# Revit family: SAL 35
name_source: partatom
category: Air Terminals
revit_build: Autodesk Revit 2017 (Build: 20160225_1515(x64)
units: mm (PartAtom-declared; Revit-internal decimal feet)

## family parameters
Always vertical = Yes
Cut with Voids When Loaded = No
Part Type = Normal
Room Calculation Point = No
Round Connector Dimension = Use Diameter
Shared = No
Work Plane-Based = No

## types (64) — shared parameters
Lw dB(A) = 30/35/40
Max Flow = 0.0 L/s
Maß A = 44 mm  [stored 0.144357 ft]
Maß C = 60 mm  [stored 0.19685 ft]
Min Flow = 0.0 L/s
Product material = RAL 9016

## per-type parameters (varying)
- 500_1-reihig mit Anschlusskasten: Gewicht (g/m)=4360; Index=1; Index L=1; Index Reihig=1; L=500 mm  [stored 1.64042 ft]; Maß B=88 mm  [stored 0.288714 ft]; Maß E=25.3 mm  [stored 0.0830052 ft]; Maß F=34 mm; Maß H=227 mm  [stored 0.744751 ft]; Maß K=36 mm  [stored 0.11811 ft]; Maß M=61 mm  [stored 0.200131 ft]; Maß Ø D=123 mm  [stored 0.403543 ft]; Maß Ø D1=121 mm  [stored 0.396982 ft]; Mindest-abstand (m)=0.5/2.7/10.5; Stutzen (Stk.)=1; Visible 1 Reihig=Yes; Visible 1 Stutzen=Yes; Visible 2 Reihig=No; Visible 2 Stutzen=No; Visible 3 Reihig=No; Visible 4 Reihig=No; x krit (m)=8.0/10.5/13.3; y (m)=1.6/2.2/2.7; Δp (Pa) 1=15/23/33; Δp (Pa) 2=21/32/45
- 500_2-reihig mit Anschlusskasten: Gewicht (g/m)=5585; Index=1; Index L=1; Index Reihig=2; L=500 mm  [stored 1.64042 ft]; Maß B=120 mm  [stored 0.393701 ft]; Maß E=57.4 mm  [stored 0.18832 ft]; Maß F=67 mm; Maß H=242 mm  [stored 0.793963 ft]; Maß K=69 mm  [stored 0.226378 ft]; Maß M=92 mm  [stored 0.301837 ft]; Maß Ø D=138 mm  [stored 0.452756 ft]; Maß Ø D1=136 mm  [stored 0.446194 ft]; Mindest-abstand (m)=3.3/12.0/>15.0; Stutzen (Stk.)=1; Visible 1 Reihig=No; Visible 1 Stutzen=Yes; Visible 2 Reihig=Yes; Visible 2 Stutzen=No; Visible 3 Reihig=No; Visible 4 Reihig=No; x krit (m)=10.6/13.8/>15.0; y (m)=2.3/2.9/3.6; Δp (Pa) 1=12/18/27; Δp (Pa) 2=18/25/36
- 500_3-reihig mit Anschlusskasten: Gewicht (g/m)=6979; Index=1; Index L=1; Index Reihig=3; L=500 mm  [stored 1.64042 ft]; Maß B=152 mm  [stored 0.498688 ft]; Maß E=89.5 mm  [stored 0.293635 ft]; Maß F=99 mm  [stored 0.324803 ft]; Maß H=262 mm  [stored 0.85958 ft]; Maß K=101 mm  [stored 0.331365 ft]; Maß M=126 mm  [stored 0.413386 ft]; Maß Ø D=158 mm; Maß Ø D1=156 mm; Mindest-abstand (m)=8.0/>15.0/>15.0; Stutzen (Stk.)=1; Visible 1 Reihig=No; Visible 1 Stutzen=Yes; Visible 2 Reihig=No; Visible 2 Stutzen=No; Visible 3 Reihig=Yes; Visible 4 Reihig=No; x krit (m)=12.3/15.0/>15.0; y (m)=2.7/3.4/4.5; Δp (Pa) 1=10/15/23; Δp (Pa) 2=15/22/33
- 500_4-reihig mit Anschlusskasten: Gewicht (g/m)=8554; Index=1; Index L=1; Index Reihig=4; L=500 mm  [stored 1.64042 ft]; Maß B=184 mm  [stored 0.603675 ft]; Maß E=121.6 mm  [stored 0.39895 ft]; Maß F=132 mm  [stored 0.433071 ft]; Maß H=302 mm  [stored 0.990814 ft]; Maß K=134 mm; Maß M=158 mm; Maß Ø D=198 mm  [stored 0.649606 ft]; Maß Ø D1=196 mm  [stored 0.643045 ft]; Mindest-abstand (m)=11.0/>15.0/>15.0; Stutzen (Stk.)=1; Visible 1 Reihig=No; Visible 1 Stutzen=Yes; Visible 2 Reihig=No; Visible 2 Stutzen=No; Visible 3 Reihig=No; Visible 4 Reihig=Yes; x krit (m)=13.4/>15.0/>15.0; y (m)=2.9/3.8/4.9; Δp (Pa) 1=9/14/21; Δp (Pa) 2=13/20/29
- 600_1-reihig mit Anschlusskasten: Gewicht (g/m)=4360; Index=1; Index L=2; Index Reihig=1; L=600 mm; Maß B=88 mm  [stored 0.288714 ft]; Maß E=25.3 mm  [stored 0.0830052 ft]; Maß F=34 mm; Maß H=227 mm  [stored 0.744751 ft]; Maß K=36 mm  [stored 0.11811 ft]; Maß M=61 mm  [stored 0.200131 ft]; Maß Ø D=123 mm  [stored 0.403543 ft]; Maß Ø D1=121 mm  [stored 0.396982 ft]; Mindest-abstand (m)=0.5/2.7/10.5; Stutzen (Stk.)=1; Visible 1 Reihig=Yes; Visible 1 Stutzen=Yes; Visible 2 Reihig=No; Visible 2 Stutzen=No; Visible 3 Reihig=No; Visible 4 Reihig=No; x krit (m)=8.0/10.5/13.3; y (m)=1.6/2.2/2.7; Δp (Pa) 1=15/23/33; Δp (Pa) 2=21/32/45
- 700_1-reihig mit Anschlusskasten: Gewicht (g/m)=4360; Index=1; Index L=3; Index Reihig=1; L=700 mm  [stored 2.29659 ft]; Maß B=88 mm  [stored 0.288714 ft]; Maß E=25.3 mm  [stored 0.0830052 ft]; Maß F=34 mm; Maß H=227 mm  [stored 0.744751 ft]; Maß K=36 mm  [stored 0.11811 ft]; Maß M=61 mm  [stored 0.200131 ft]; Maß Ø D=123 mm  [stored 0.403543 ft]; Maß Ø D1=121 mm  [stored 0.396982 ft]; Mindest-abstand (m)=0.5/2.7/10.5; Stutzen (Stk.)=1; Visible 1 Reihig=Yes; Visible 1 Stutzen=Yes; Visible 2 Reihig=No; Visible 2 Stutzen=No; Visible 3 Reihig=No; Visible 4 Reihig=No; x krit (m)=8.0/10.5/13.3; y (m)=1.6/2.2/2.7; Δp (Pa) 1=15/23/33; Δp (Pa) 2=21/32/45
- 800_1-reihig mit Anschlusskasten: Gewicht (g/m)=4360; Index=1; Index L=4; Index Reihig=1; L=800 mm  [stored 2.62467 ft]; Maß B=88 mm  [stored 0.288714 ft]; Maß E=25.3 mm  [stored 0.0830052 ft]; Maß F=34 mm; Maß H=227 mm  [stored 0.744751 ft]; Maß K=36 mm  [stored 0.11811 ft]; Maß M=61 mm  [stored 0.200131 ft]; Maß Ø D=123 mm  [stored 0.403543 ft]; Maß Ø D1=121 mm  [stored 0.396982 ft]; Mindest-abstand (m)=0.5/2.7/10.5; Stutzen (Stk.)=1; Visible 1 Reihig=Yes; Visible 1 Stutzen=Yes; Visible 2 Reihig=No; Visible 2 Stutzen=No; Visible 3 Reihig=No; Visible 4 Reihig=No; x krit (m)=8.0/10.5/13.3; y (m)=1.6/2.2/2.7; Δp (Pa) 1=15/23/33; Δp (Pa) 2=21/32/45
- 900_1-reihig mit Anschlusskasten: Gewicht (g/m)=4360; Index=1; Index L=5; Index Reihig=1; L=900 mm  [stored 2.95276 ft]; Maß B=88 mm  [stored 0.288714 ft]; Maß E=25.3 mm  [stored 0.0830052 ft]; Maß F=34 mm; Maß H=227 mm  [stored 0.744751 ft]; Maß K=36 mm  [stored 0.11811 ft]; Maß M=61 mm  [stored 0.200131 ft]; Maß Ø D=123 mm  [stored 0.403543 ft]; Maß Ø D1=121 mm  [stored 0.396982 ft]; Mindest-abstand (m)=0.5/2.7/10.5; Stutzen (Stk.)=1; Visible 1 Reihig=Yes; Visible 1 Stutzen=Yes; Visible 2 Reihig=No; Visible 2 Stutzen=No; Visible 3 Reihig=No; Visible 4 Reihig=No; x krit (m)=8.0/10.5/13.3; y (m)=1.6/2.2/2.7; Δp (Pa) 1=15/23/33; Δp (Pa) 2=21/32/45
- 1000_1-reihig mit Anschlusskasten: Gewicht (g/m)=4360; Index=1; Index L=6; Index Reihig=1; L=1000 mm  [stored 3.28084 ft]; Maß B=88 mm  [stored 0.288714 ft]; Maß E=25.3 mm  [stored 0.0830052 ft]; Maß F=34 mm; Maß H=227 mm  [stored 0.744751 ft]; Maß K=36 mm  [stored 0.11811 ft]; Maß M=61 mm  [stored 0.200131 ft]; Maß Ø D=123 mm  [stored 0.403543 ft]; Maß Ø D1=121 mm  [stored 0.396982 ft]; Mindest-abstand (m)=0.5/2.7/10.5; Stutzen (Stk.)=1; Visible 1 Reihig=Yes; Visible 1 Stutzen=Yes; Visible 2 Reihig=No; Visible 2 Stutzen=No; Visible 3 Reihig=No; Visible 4 Reihig=No; x krit (m)=8.0/10.5/13.3; y (m)=1.6/2.2/2.7; Δp (Pa) 1=15/23/33; Δp (Pa) 2=21/32/45
- 1100_1-reihig mit Anschlusskasten: Gewicht (g/m)=4360; Index=1; Index L=7; Index Reihig=1; L=1100 mm; Maß B=88 mm  [stored 0.288714 ft]; Maß E=25.3 mm  [stored 0.0830052 ft]; Maß F=34 mm; Maß H=227 mm  [stored 0.744751 ft]; Maß K=36 mm  [stored 0.11811 ft]; Maß M=61 mm  [stored 0.200131 ft]; Maß Ø D=123 mm  [stored 0.403543 ft]; Maß Ø D1=121 mm  [stored 0.396982 ft]; Mindest-abstand (m)=0.5/2.7/10.5; Stutzen (Stk.)=1; Visible 1 Reihig=Yes; Visible 1 Stutzen=Yes; Visible 2 Reihig=No; Visible 2 Stutzen=No; Visible 3 Reihig=No; Visible 4 Reihig=No; x krit (m)=8.0/10.5/13.3; y (m)=1.6/2.2/2.7; Δp (Pa) 1=15/23/33; Δp (Pa) 2=21/32/45
- 1200_1-reihig mit Anschlusskasten: Gewicht (g/m)=4360; Index=1; Index L=8; Index Reihig=1; L=1200 mm; Maß B=88 mm  [stored 0.288714 ft]; Maß E=25.3 mm  [stored 0.0830052 ft]; Maß F=34 mm; Maß H=227 mm  [stored 0.744751 ft]; Maß K=36 mm  [stored 0.11811 ft]; Maß M=61 mm  [stored 0.200131 ft]; Maß Ø D=123 mm  [stored 0.403543 ft]; Maß Ø D1=121 mm  [stored 0.396982 ft]; Mindest-abstand (m)=0.5/2.7/10.5; Stutzen (Stk.)=1; Visible 1 Reihig=Yes; Visible 1 Stutzen=Yes; Visible 2 Reihig=No; Visible 2 Stutzen=No; Visible 3 Reihig=No; Visible 4 Reihig=No; x krit (m)=8.0/10.5/13.3; y (m)=1.6/2.2/2.7; Δp (Pa) 1=15/23/33; Δp (Pa) 2=21/32/45
- 1300_1-reihig mit Anschlusskasten: Gewicht (g/m)=4360; Index=1; Index L=9; Index Reihig=1; L=1300 mm; Maß B=88 mm  [stored 0.288714 ft]; Maß E=25.3 mm  [stored 0.0830052 ft]; Maß F=34 mm; Maß H=227 mm  [stored 0.744751 ft]; Maß K=36 mm  [stored 0.11811 ft]; Maß M=61 mm  [stored 0.200131 ft]; Maß Ø D=123 mm  [stored 0.403543 ft]; Maß Ø D1=121 mm  [stored 0.396982 ft]; Mindest-abstand (m)=0.5/2.7/10.5; Stutzen (Stk.)=1; Visible 1 Reihig=Yes; Visible 1 Stutzen=Yes; Visible 2 Reihig=No; Visible 2 Stutzen=No; Visible 3 Reihig=No; Visible 4 Reihig=No; x krit (m)=8.0/10.5/13.3; y (m)=1.6/2.2/2.7; Δp (Pa) 1=15/23/33; Δp (Pa) 2=21/32/45
- 1400_1-reihig mit Anschlusskasten: Gewicht (g/m)=4360; Index=1; Index L=10; Index Reihig=1; L=1400 mm; Maß B=88 mm  [stored 0.288714 ft]; Maß E=25.3 mm  [stored 0.0830052 ft]; Maß F=34 mm; Maß H=227 mm  [stored 0.744751 ft]; Maß K=36 mm  [stored 0.11811 ft]; Maß M=61 mm  [stored 0.200131 ft]; Maß Ø D=123 mm  [stored 0.403543 ft]; Maß Ø D1=121 mm  [stored 0.396982 ft]; Mindest-abstand (m)=0.5/2.7/10.5; Stutzen (Stk.)=1; Visible 1 Reihig=Yes; Visible 1 Stutzen=Yes; Visible 2 Reihig=No; Visible 2 Stutzen=No; Visible 3 Reihig=No; Visible 4 Reihig=No; x krit (m)=8.0/10.5/13.3; y (m)=1.6/2.2/2.7; Δp (Pa) 1=15/23/33; Δp (Pa) 2=21/32/45
- 1500_1-reihig mit Anschlusskasten: Gewicht (g/m)=4360; Index=1; Index L=11; Index Reihig=1; L=1500 mm; Maß B=88 mm  [stored 0.288714 ft]; Maß E=25.3 mm  [stored 0.0830052 ft]; Maß F=34 mm; Maß H=227 mm  [stored 0.744751 ft]; Maß K=36 mm  [stored 0.11811 ft]; Maß M=61 mm  [stored 0.200131 ft]; Maß Ø D=123 mm  [stored 0.403543 ft]; Maß Ø D1=121 mm  [stored 0.396982 ft]; Mindest-abstand (m)=0.5/2.7/10.5; Stutzen (Stk.)=1; Visible 1 Reihig=Yes; Visible 1 Stutzen=Yes; Visible 2 Reihig=No; Visible 2 Stutzen=No; Visible 3 Reihig=No; Visible 4 Reihig=No; x krit (m)=8.0/10.5/13.3; y (m)=1.6/2.2/2.7; Δp (Pa) 1=15/23/33; Δp (Pa) 2=21/32/45
- 1600_1-reihig mit Anschlusskasten: Gewicht (g/m)=4360; Index=2; Index L=12; Index Reihig=1; L=1600 mm; Maß B=88 mm  [stored 0.288714 ft]; Maß E=25.3 mm  [stored 0.0830052 ft]; Maß F=34 mm; Maß H=227 mm  [stored 0.744751 ft]; Maß K=36 mm  [stored 0.11811 ft]; Maß M=61 mm  [stored 0.200131 ft]; Maß Ø D=123 mm  [stored 0.403543 ft]; Maß Ø D1=121 mm  [stored 0.396982 ft]; Mindest-abstand (m)=0.5/2.7/10.5; Stutzen (Stk.)=2; Visible 1 Reihig=Yes; Visible 1 Stutzen=No; Visible 2 Reihig=No; Visible 2 Stutzen=Yes; Visible 3 Reihig=No; Visible 4 Reihig=No; x krit (m)=8.0/10.5/13.3; y (m)=1.6/2.2/2.7; Δp (Pa) 1=15/23/33; Δp (Pa) 2=21/32/45
- 1700_1-reihig mit Anschlusskasten: Gewicht (g/m)=4360; Index=2; Index L=13; Index Reihig=1; L=1700 mm; Maß B=88 mm  [stored 0.288714 ft]; Maß E=25.3 mm  [stored 0.0830052 ft]; Maß F=34 mm; Maß H=227 mm  [stored 0.744751 ft]; Maß K=36 mm  [stored 0.11811 ft]; Maß M=61 mm  [stored 0.200131 ft]; Maß Ø D=123 mm  [stored 0.403543 ft]; Maß Ø D1=121 mm  [stored 0.396982 ft]; Mindest-abstand (m)=0.5/2.7/10.5; Stutzen (Stk.)=2; Visible 1 Reihig=Yes; Visible 1 Stutzen=No; Visible 2 Reihig=No; Visible 2 Stutzen=Yes; Visible 3 Reihig=No; Visible 4 Reihig=No; x krit (m)=8.0/10.5/13.3; y (m)=1.6/2.2/2.7; Δp (Pa) 1=15/23/33; Δp (Pa) 2=21/32/45
- 1800_1-reihig mit Anschlusskasten: Gewicht (g/m)=4360; Index=2; Index L=14; Index Reihig=1; L=1800 mm; Maß B=88 mm  [stored 0.288714 ft]; Maß E=25.3 mm  [stored 0.0830052 ft]; Maß F=34 mm; Maß H=227 mm  [stored 0.744751 ft]; Maß K=36 mm  [stored 0.11811 ft]; Maß M=61 mm  [stored 0.200131 ft]; Maß Ø D=123 mm  [stored 0.403543 ft]; Maß Ø D1=121 mm  [stored 0.396982 ft]; Mindest-abstand (m)=0.5/2.7/10.5; Stutzen (Stk.)=2; Visible 1 Reihig=Yes; Visible 1 Stutzen=No; Visible 2 Reihig=No; Visible 2 Stutzen=Yes; Visible 3 Reihig=No; Visible 4 Reihig=No; x krit (m)=8.0/10.5/13.3; y (m)=1.6/2.2/2.7; Δp (Pa) 1=15/23/33; Δp (Pa) 2=21/32/45
- 1900_1-reihig mit Anschlusskasten: Gewicht (g/m)=4360; Index=2; Index L=15; Index Reihig=1; L=1900 mm; Maß B=88 mm  [stored 0.288714 ft]; Maß E=25.3 mm  [stored 0.0830052 ft]; Maß F=34 mm; Maß H=227 mm  [stored 0.744751 ft]; Maß K=36 mm  [stored 0.11811 ft]; Maß M=61 mm  [stored 0.200131 ft]; Maß Ø D=123 mm  [stored 0.403543 ft]; Maß Ø D1=121 mm  [stored 0.396982 ft]; Mindest-abstand (m)=0.5/2.7/10.5; Stutzen (Stk.)=2; Visible 1 Reihig=Yes; Visible 1 Stutzen=No; Visible 2 Reihig=No; Visible 2 Stutzen=Yes; Visible 3 Reihig=No; Visible 4 Reihig=No; x krit (m)=8.0/10.5/13.3; y (m)=1.6/2.2/2.7; Δp (Pa) 1=15/23/33; Δp (Pa) 2=21/32/45
- 2000_1-reihig mit Anschlusskasten: Gewicht (g/m)=4360; Index=2; Index L=16; Index Reihig=1; L=2000 mm; Maß B=88 mm  [stored 0.288714 ft]; Maß E=25.3 mm  [stored 0.0830052 ft]; Maß F=34 mm; Maß H=227 mm  [stored 0.744751 ft]; Maß K=36 mm  [stored 0.11811 ft]; Maß M=61 mm  [stored 0.200131 ft]; Maß Ø D=123 mm  [stored 0.403543 ft]; Maß Ø D1=121 mm  [stored 0.396982 ft]; Mindest-abstand (m)=0.5/2.7/10.5; Stutzen (Stk.)=2; Visible 1 Reihig=Yes; Visible 1 Stutzen=No; Visible 2 Reihig=No; Visible 2 Stutzen=Yes; Visible 3 Reihig=No; Visible 4 Reihig=No; x krit (m)=8.0/10.5/13.3; y (m)=1.6/2.2/2.7; Δp (Pa) 1=15/23/33; Δp (Pa) 2=21/32/45
- 600_2-reihig mit Anschlusskasten: Gewicht (g/m)=5585; Index=1; Index L=2; Index Reihig=2; L=600 mm; Maß B=120 mm  [stored 0.393701 ft]; Maß E=57.4 mm  [stored 0.18832 ft]; Maß F=67 mm; Maß H=242 mm  [stored 0.793963 ft]; Maß K=69 mm  [stored 0.226378 ft]; Maß M=92 mm  [stored 0.301837 ft]; Maß Ø D=138 mm  [stored 0.452756 ft]; Maß Ø D1=136 mm  [stored 0.446194 ft]; Mindest-abstand (m)=3.3/12.0/>15.0; Stutzen (Stk.)=1; Visible 1 Reihig=No; Visible 1 Stutzen=Yes; Visible 2 Reihig=Yes; Visible 2 Stutzen=No; Visible 3 Reihig=No; Visible 4 Reihig=No; x krit (m)=10.6/13.8/>15.0; y (m)=2.3/2.9/3.6; Δp (Pa) 1=12/18/27; Δp (Pa) 2=18/25/36
- 600_3-reihig mit Anschlusskasten: Gewicht (g/m)=6979; Index=1; Index L=2; Index Reihig=3; L=600 mm; Maß B=152 mm  [stored 0.498688 ft]; Maß E=89.5 mm  [stored 0.293635 ft]; Maß F=99 mm  [stored 0.324803 ft]; Maß H=262 mm  [stored 0.85958 ft]; Maß K=101 mm  [stored 0.331365 ft]; Maß M=126 mm  [stored 0.413386 ft]; Maß Ø D=158 mm; Maß Ø D1=156 mm; Mindest-abstand (m)=8.0/>15.0/>15.0; Stutzen (Stk.)=1; Visible 1 Reihig=No; Visible 1 Stutzen=Yes; Visible 2 Reihig=No; Visible 2 Stutzen=No; Visible 3 Reihig=Yes; Visible 4 Reihig=No; x krit (m)=12.3/15.0/>15.0; y (m)=2.7/3.4/4.5; Δp (Pa) 1=10/15/23; Δp (Pa) 2=15/22/33
- 600_4-reihig mit Anschlusskasten: Gewicht (g/m)=8554; Index=1; Index L=2; Index Reihig=4; L=600 mm; Maß B=184 mm  [stored 0.603675 ft]; Maß E=121.6 mm  [stored 0.39895 ft]; Maß F=132 mm  [stored 0.433071 ft]; Maß H=302 mm  [stored 0.990814 ft]; Maß K=134 mm; Maß M=158 mm; Maß Ø D=198 mm  [stored 0.649606 ft]; Maß Ø D1=196 mm  [stored 0.643045 ft]; Mindest-abstand (m)=11.0/>15.0/>15.0; Stutzen (Stk.)=1; Visible 1 Reihig=No; Visible 1 Stutzen=Yes; Visible 2 Reihig=No; Visible 2 Stutzen=No; Visible 3 Reihig=No; Visible 4 Reihig=Yes; x krit (m)=13.4/>15.0/>15.0; y (m)=2.9/3.8/4.9; Δp (Pa) 1=9/14/21; Δp (Pa) 2=13/20/29
- 700_2-reihig mit Anschlusskasten: Gewicht (g/m)=5585; Index=1; Index L=3; Index Reihig=2; L=700 mm  [stored 2.29659 ft]; Maß B=120 mm  [stored 0.393701 ft]; Maß E=57.4 mm  [stored 0.18832 ft]; Maß F=67 mm; Maß H=242 mm  [stored 0.793963 ft]; Maß K=69 mm  [stored 0.226378 ft]; Maß M=92 mm  [stored 0.301837 ft]; Maß Ø D=138 mm  [stored 0.452756 ft]; Maß Ø D1=136 mm  [stored 0.446194 ft]; Mindest-abstand (m)=3.3/12.0/>15.0; Stutzen (Stk.)=1; Visible 1 Reihig=No; Visible 1 Stutzen=Yes; Visible 2 Reihig=Yes; Visible 2 Stutzen=No; Visible 3 Reihig=No; Visible 4 Reihig=No; x krit (m)=10.6/13.8/>15.0; y (m)=2.3/2.9/3.6; Δp (Pa) 1=12/18/27; Δp (Pa) 2=18/25/36
- 700_3-reihig mit Anschlusskasten: Gewicht (g/m)=6979; Index=1; Index L=3; Index Reihig=3; L=700 mm  [stored 2.29659 ft]; Maß B=152 mm  [stored 0.498688 ft]; Maß E=89.5 mm  [stored 0.293635 ft]; Maß F=99 mm  [stored 0.324803 ft]; Maß H=262 mm  [stored 0.85958 ft]; Maß K=101 mm  [stored 0.331365 ft]; Maß M=126 mm  [stored 0.413386 ft]; Maß Ø D=158 mm; Maß Ø D1=156 mm; Mindest-abstand (m)=8.0/>15.0/>15.0; Stutzen (Stk.)=1; Visible 1 Reihig=No; Visible 1 Stutzen=Yes; Visible 2 Reihig=No; Visible 2 Stutzen=No; Visible 3 Reihig=Yes; Visible 4 Reihig=No; x krit (m)=12.3/15.0/>15.0; y (m)=2.7/3.4/4.5; Δp (Pa) 1=10/15/23; Δp (Pa) 2=15/22/33
- 700_4-reihig mit Anschlusskasten: Gewicht (g/m)=8554; Index=1; Index L=3; Index Reihig=4; L=700 mm  [stored 2.29659 ft]; Maß B=184 mm  [stored 0.603675 ft]; Maß E=121.6 mm  [stored 0.39895 ft]; Maß F=132 mm  [stored 0.433071 ft]; Maß H=302 mm  [stored 0.990814 ft]; Maß K=134 mm; Maß M=158 mm; Maß Ø D=198 mm  [stored 0.649606 ft]; Maß Ø D1=196 mm  [stored 0.643045 ft]; Mindest-abstand (m)=11.0/>15.0/>15.0; Stutzen (Stk.)=1; Visible 1 Reihig=No; Visible 1 Stutzen=Yes; Visible 2 Reihig=No; Visible 2 Stutzen=No; Visible 3 Reihig=No; Visible 4 Reihig=Yes; x krit (m)=13.4/>15.0/>15.0; y (m)=2.9/3.8/4.9; Δp (Pa) 1=9/14/21; Δp (Pa) 2=13/20/29
- 800_2-reihig mit Anschlusskasten: Gewicht (g/m)=5585; Index=1; Index L=4; Index Reihig=2; L=800 mm  [stored 2.62467 ft]; Maß B=120 mm  [stored 0.393701 ft]; Maß E=57.4 mm  [stored 0.18832 ft]; Maß F=67 mm; Maß H=242 mm  [stored 0.793963 ft]; Maß K=69 mm  [stored 0.226378 ft]; Maß M=92 mm  [stored 0.301837 ft]; Maß Ø D=138 mm  [stored 0.452756 ft]; Maß Ø D1=136 mm  [stored 0.446194 ft]; Mindest-abstand (m)=3.3/12.0/>15.0; Stutzen (Stk.)=1; Visible 1 Reihig=No; Visible 1 Stutzen=Yes; Visible 2 Reihig=Yes; Visible 2 Stutzen=No; Visible 3 Reihig=No; Visible 4 Reihig=No; x krit (m)=10.6/13.8/>15.0; y (m)=2.3/2.9/3.6; Δp (Pa) 1=12/18/27; Δp (Pa) 2=18/25/36
- 800_3-reihig mit Anschlusskasten: Gewicht (g/m)=6979; Index=1; Index L=4; Index Reihig=3; L=800 mm  [stored 2.62467 ft]; Maß B=152 mm  [stored 0.498688 ft]; Maß E=89.5 mm  [stored 0.293635 ft]; Maß F=99 mm  [stored 0.324803 ft]; Maß H=262 mm  [stored 0.85958 ft]; Maß K=101 mm  [stored 0.331365 ft]; Maß M=126 mm  [stored 0.413386 ft]; Maß Ø D=158 mm; Maß Ø D1=156 mm; Mindest-abstand (m)=8.0/>15.0/>15.0; Stutzen (Stk.)=1; Visible 1 Reihig=No; Visible 1 Stutzen=Yes; Visible 2 Reihig=No; Visible 2 Stutzen=No; Visible 3 Reihig=Yes; Visible 4 Reihig=No; x krit (m)=12.3/15.0/>15.0; y (m)=2.7/3.4/4.5; Δp (Pa) 1=10/15/23; Δp (Pa) 2=15/22/33
- 800_4-reihig mit Anschlusskasten: Gewicht (g/m)=8554; Index=1; Index L=4; Index Reihig=4; L=800 mm  [stored 2.62467 ft]; Maß B=184 mm  [stored 0.603675 ft]; Maß E=121.6 mm  [stored 0.39895 ft]; Maß F=132 mm  [stored 0.433071 ft]; Maß H=302 mm  [stored 0.990814 ft]; Maß K=134 mm; Maß M=158 mm; Maß Ø D=198 mm  [stored 0.649606 ft]; Maß Ø D1=196 mm  [stored 0.643045 ft]; Mindest-abstand (m)=11.0/>15.0/>15.0; Stutzen (Stk.)=1; Visible 1 Reihig=No; Visible 1 Stutzen=Yes; Visible 2 Reihig=No; Visible 2 Stutzen=No; Visible 3 Reihig=No; Visible 4 Reihig=Yes; x krit (m)=13.4/>15.0/>15.0; y (m)=2.9/3.8/4.9; Δp (Pa) 1=9/14/21; Δp (Pa) 2=13/20/29
- 900_2-reihig mit Anschlusskasten: Gewicht (g/m)=5585; Index=1; Index L=5; Index Reihig=2; L=900 mm  [stored 2.95276 ft]; Maß B=120 mm  [stored 0.393701 ft]; Maß E=57.4 mm  [stored 0.18832 ft]; Maß F=67 mm; Maß H=242 mm  [stored 0.793963 ft]; Maß K=69 mm  [stored 0.226378 ft]; Maß M=92 mm  [stored 0.301837 ft]; Maß Ø D=138 mm  [stored 0.452756 ft]; Maß Ø D1=136 mm  [stored 0.446194 ft]; Mindest-abstand (m)=3.3/12.0/>15.0; Stutzen (Stk.)=1; Visible 1 Reihig=No; Visible 1 Stutzen=Yes; Visible 2 Reihig=Yes; Visible 2 Stutzen=No; Visible 3 Reihig=No; Visible 4 Reihig=No; x krit (m)=10.6/13.8/>15.0; y (m)=2.3/2.9/3.6; Δp (Pa) 1=12/18/27; Δp (Pa) 2=18/25/36
- 900_3-reihig mit Anschlusskasten: Gewicht (g/m)=6979; Index=1; Index L=5; Index Reihig=3; L=900 mm  [stored 2.95276 ft]; Maß B=152 mm  [stored 0.498688 ft]; Maß E=89.5 mm  [stored 0.293635 ft]; Maß F=99 mm  [stored 0.324803 ft]; Maß H=262 mm  [stored 0.85958 ft]; Maß K=101 mm  [stored 0.331365 ft]; Maß M=126 mm  [stored 0.413386 ft]; Maß Ø D=158 mm; Maß Ø D1=156 mm; Mindest-abstand (m)=8.0/>15.0/>15.0; Stutzen (Stk.)=1; Visible 1 Reihig=No; Visible 1 Stutzen=Yes; Visible 2 Reihig=No; Visible 2 Stutzen=No; Visible 3 Reihig=Yes; Visible 4 Reihig=No; x krit (m)=12.3/15.0/>15.0; y (m)=2.7/3.4/4.5; Δp (Pa) 1=10/15/23; Δp (Pa) 2=15/22/33
- 900_4-reihig mit Anschlusskasten: Gewicht (g/m)=8554; Index=1; Index L=5; Index Reihig=4; L=900 mm  [stored 2.95276 ft]; Maß B=184 mm  [stored 0.603675 ft]; Maß E=121.6 mm  [stored 0.39895 ft]; Maß F=132 mm  [stored 0.433071 ft]; Maß H=302 mm  [stored 0.990814 ft]; Maß K=134 mm; Maß M=158 mm; Maß Ø D=198 mm  [stored 0.649606 ft]; Maß Ø D1=196 mm  [stored 0.643045 ft]; Mindest-abstand (m)=11.0/>15.0/>15.0; Stutzen (Stk.)=1; Visible 1 Reihig=No; Visible 1 Stutzen=Yes; Visible 2 Reihig=No; Visible 2 Stutzen=No; Visible 3 Reihig=No; Visible 4 Reihig=Yes; x krit (m)=13.4/>15.0/>15.0; y (m)=2.9/3.8/4.9; Δp (Pa) 1=9/14/21; Δp (Pa) 2=13/20/29
- 1000_2-reihig mit Anschlusskasten: Gewicht (g/m)=5585; Index=1; Index L=6; Index Reihig=2; L=1000 mm  [stored 3.28084 ft]; Maß B=120 mm  [stored 0.393701 ft]; Maß E=57.4 mm  [stored 0.18832 ft]; Maß F=67 mm; Maß H=242 mm  [stored 0.793963 ft]; Maß K=69 mm  [stored 0.226378 ft]; Maß M=92 mm  [stored 0.301837 ft]; Maß Ø D=138 mm  [stored 0.452756 ft]; Maß Ø D1=136 mm  [stored 0.446194 ft]; Mindest-abstand (m)=3.3/12.0/>15.0; Stutzen (Stk.)=1; Visible 1 Reihig=No; Visible 1 Stutzen=Yes; Visible 2 Reihig=Yes; Visible 2 Stutzen=No; Visible 3 Reihig=No; Visible 4 Reihig=No; x krit (m)=10.6/13.8/>15.0; y (m)=2.3/2.9/3.6; Δp (Pa) 1=12/18/27; Δp (Pa) 2=18/25/36
- 1000_3-reihig mit Anschlusskasten: Gewicht (g/m)=6979; Index=1; Index L=6; Index Reihig=3; L=1000 mm  [stored 3.28084 ft]; Maß B=152 mm  [stored 0.498688 ft]; Maß E=89.5 mm  [stored 0.293635 ft]; Maß F=99 mm  [stored 0.324803 ft]; Maß H=262 mm  [stored 0.85958 ft]; Maß K=101 mm  [stored 0.331365 ft]; Maß M=126 mm  [stored 0.413386 ft]; Maß Ø D=158 mm; Maß Ø D1=156 mm; Mindest-abstand (m)=8.0/>15.0/>15.0; Stutzen (Stk.)=1; Visible 1 Reihig=No; Visible 1 Stutzen=Yes; Visible 2 Reihig=No; Visible 2 Stutzen=No; Visible 3 Reihig=Yes; Visible 4 Reihig=No; x krit (m)=12.3/15.0/>15.0; y (m)=2.7/3.4/4.5; Δp (Pa) 1=10/15/23; Δp (Pa) 2=15/22/33
- 1000_4-reihig mit Anschlusskasten: Gewicht (g/m)=8554; Index=1; Index L=6; Index Reihig=4; L=1000 mm  [stored 3.28084 ft]; Maß B=184 mm  [stored 0.603675 ft]; Maß E=121.6 mm  [stored 0.39895 ft]; Maß F=132 mm  [stored 0.433071 ft]; Maß H=302 mm  [stored 0.990814 ft]; Maß K=134 mm; Maß M=158 mm; Maß Ø D=198 mm  [stored 0.649606 ft]; Maß Ø D1=196 mm  [stored 0.643045 ft]; Mindest-abstand (m)=11.0/>15.0/>15.0; Stutzen (Stk.)=1; Visible 1 Reihig=No; Visible 1 Stutzen=Yes; Visible 2 Reihig=No; Visible 2 Stutzen=No; Visible 3 Reihig=No; Visible 4 Reihig=Yes; x krit (m)=13.4/>15.0/>15.0; y (m)=2.9/3.8/4.9; Δp (Pa) 1=9/14/21; Δp (Pa) 2=13/20/29
- 1100_2-reihig mit Anschlusskasten: Gewicht (g/m)=5585; Index=1; Index L=7; Index Reihig=2; L=1100 mm; Maß B=120 mm  [stored 0.393701 ft]; Maß E=57.4 mm  [stored 0.18832 ft]; Maß F=67 mm; Maß H=242 mm  [stored 0.793963 ft]; Maß K=69 mm  [stored 0.226378 ft]; Maß M=92 mm  [stored 0.301837 ft]; Maß Ø D=138 mm  [stored 0.452756 ft]; Maß Ø D1=136 mm  [stored 0.446194 ft]; Mindest-abstand (m)=3.3/12.0/>15.0; Stutzen (Stk.)=1; Visible 1 Reihig=No; Visible 1 Stutzen=Yes; Visible 2 Reihig=Yes; Visible 2 Stutzen=No; Visible 3 Reihig=No; Visible 4 Reihig=No; x krit (m)=10.6/13.8/>15.0; y (m)=2.3/2.9/3.6; Δp (Pa) 1=12/18/27; Δp (Pa) 2=18/25/36
- 1100_3-reihig mit Anschlusskasten: Gewicht (g/m)=6979; Index=1; Index L=7; Index Reihig=3; L=1100 mm; Maß B=152 mm  [stored 0.498688 ft]; Maß E=89.5 mm  [stored 0.293635 ft]; Maß F=99 mm  [stored 0.324803 ft]; Maß H=262 mm  [stored 0.85958 ft]; Maß K=101 mm  [stored 0.331365 ft]; Maß M=126 mm  [stored 0.413386 ft]; Maß Ø D=158 mm; Maß Ø D1=156 mm; Mindest-abstand (m)=8.0/>15.0/>15.0; Stutzen (Stk.)=1; Visible 1 Reihig=No; Visible 1 Stutzen=Yes; Visible 2 Reihig=No; Visible 2 Stutzen=No; Visible 3 Reihig=Yes; Visible 4 Reihig=No; x krit (m)=12.3/15.0/>15.0; y (m)=2.7/3.4/4.5; Δp (Pa) 1=10/15/23; Δp (Pa) 2=15/22/33
- 1100_4-reihig mit Anschlusskasten: Gewicht (g/m)=8554; Index=1; Index L=7; Index Reihig=4; L=1100 mm; Maß B=184 mm  [stored 0.603675 ft]; Maß E=121.6 mm  [stored 0.39895 ft]; Maß F=132 mm  [stored 0.433071 ft]; Maß H=302 mm  [stored 0.990814 ft]; Maß K=134 mm; Maß M=158 mm; Maß Ø D=198 mm  [stored 0.649606 ft]; Maß Ø D1=196 mm  [stored 0.643045 ft]; Mindest-abstand (m)=11.0/>15.0/>15.0; Stutzen (Stk.)=1; Visible 1 Reihig=No; Visible 1 Stutzen=Yes; Visible 2 Reihig=No; Visible 2 Stutzen=No; Visible 3 Reihig=No; Visible 4 Reihig=Yes; x krit (m)=13.4/>15.0/>15.0; y (m)=2.9/3.8/4.9; Δp (Pa) 1=9/14/21; Δp (Pa) 2=13/20/29
- 1200_2-reihig mit Anschlusskasten: Gewicht (g/m)=5585; Index=1; Index L=8; Index Reihig=2; L=1200 mm; Maß B=120 mm  [stored 0.393701 ft]; Maß E=57.4 mm  [stored 0.18832 ft]; Maß F=67 mm; Maß H=242 mm  [stored 0.793963 ft]; Maß K=69 mm  [stored 0.226378 ft]; Maß M=92 mm  [stored 0.301837 ft]; Maß Ø D=138 mm  [stored 0.452756 ft]; Maß Ø D1=136 mm  [stored 0.446194 ft]; Mindest-abstand (m)=3.3/12.0/>15.0; Stutzen (Stk.)=1; Visible 1 Reihig=No; Visible 1 Stutzen=Yes; Visible 2 Reihig=Yes; Visible 2 Stutzen=No; Visible 3 Reihig=No; Visible 4 Reihig=No; x krit (m)=10.6/13.8/>15.0; y (m)=2.3/2.9/3.6; Δp (Pa) 1=12/18/27; Δp (Pa) 2=18/25/36
- 1200_3-reihig mit Anschlusskasten: Gewicht (g/m)=6979; Index=1; Index L=8; Index Reihig=3; L=1200 mm; Maß B=152 mm  [stored 0.498688 ft]; Maß E=89.5 mm  [stored 0.293635 ft]; Maß F=99 mm  [stored 0.324803 ft]; Maß H=262 mm  [stored 0.85958 ft]; Maß K=101 mm  [stored 0.331365 ft]; Maß M=126 mm  [stored 0.413386 ft]; Maß Ø D=158 mm; Maß Ø D1=156 mm; Mindest-abstand (m)=8.0/>15.0/>15.0; Stutzen (Stk.)=1; Visible 1 Reihig=No; Visible 1 Stutzen=Yes; Visible 2 Reihig=No; Visible 2 Stutzen=No; Visible 3 Reihig=Yes; Visible 4 Reihig=No; x krit (m)=12.3/15.0/>15.0; y (m)=2.7/3.4/4.5; Δp (Pa) 1=10/15/23; Δp (Pa) 2=15/22/33
- 1200_4-reihig mit Anschlusskasten: Gewicht (g/m)=8554; Index=1; Index L=8; Index Reihig=4; L=1200 mm; Maß B=184 mm  [stored 0.603675 ft]; Maß E=121.6 mm  [stored 0.39895 ft]; Maß F=132 mm  [stored 0.433071 ft]; Maß H=302 mm  [stored 0.990814 ft]; Maß K=134 mm; Maß M=158 mm; Maß Ø D=198 mm  [stored 0.649606 ft]; Maß Ø D1=196 mm  [stored 0.643045 ft]; Mindest-abstand (m)=11.0/>15.0/>15.0; Stutzen (Stk.)=1; Visible 1 Reihig=No; Visible 1 Stutzen=Yes; Visible 2 Reihig=No; Visible 2 Stutzen=No; Visible 3 Reihig=No; Visible 4 Reihig=Yes; x krit (m)=13.4/>15.0/>15.0; y (m)=2.9/3.8/4.9; Δp (Pa) 1=9/14/21; Δp (Pa) 2=13/20/29
- 1300_2-reihig mit Anschlusskasten: Gewicht (g/m)=5585; Index=1; Index L=9; Index Reihig=2; L=1300 mm; Maß B=120 mm  [stored 0.393701 ft]; Maß E=57.4 mm  [stored 0.18832 ft]; Maß F=67 mm; Maß H=242 mm  [stored 0.793963 ft]; Maß K=69 mm  [stored 0.226378 ft]; Maß M=92 mm  [stored 0.301837 ft]; Maß Ø D=138 mm  [stored 0.452756 ft]; Maß Ø D1=136 mm  [stored 0.446194 ft]; Mindest-abstand (m)=3.3/12.0/>15.0; Stutzen (Stk.)=1; Visible 1 Reihig=No; Visible 1 Stutzen=Yes; Visible 2 Reihig=Yes; Visible 2 Stutzen=No; Visible 3 Reihig=No; Visible 4 Reihig=No; x krit (m)=10.6/13.8/>15.0; y (m)=2.3/2.9/3.6; Δp (Pa) 1=12/18/27; Δp (Pa) 2=18/25/36
- 1300_3-reihig mit Anschlusskasten: Gewicht (g/m)=6979; Index=1; Index L=9; Index Reihig=3; L=1300 mm; Maß B=152 mm  [stored 0.498688 ft]; Maß E=89.5 mm  [stored 0.293635 ft]; Maß F=99 mm  [stored 0.324803 ft]; Maß H=262 mm  [stored 0.85958 ft]; Maß K=101 mm  [stored 0.331365 ft]; Maß M=126 mm  [stored 0.413386 ft]; Maß Ø D=158 mm; Maß Ø D1=156 mm; Mindest-abstand (m)=8.0/>15.0/>15.0; Stutzen (Stk.)=1; Visible 1 Reihig=No; Visible 1 Stutzen=Yes; Visible 2 Reihig=No; Visible 2 Stutzen=No; Visible 3 Reihig=Yes; Visible 4 Reihig=No; x krit (m)=12.3/15.0/>15.0; y (m)=2.7/3.4/4.5; Δp (Pa) 1=10/15/23; Δp (Pa) 2=15/22/33
- 1300_4-reihig mit Anschlusskasten: Gewicht (g/m)=8554; Index=1; Index L=9; Index Reihig=4; L=1300 mm; Maß B=184 mm  [stored 0.603675 ft]; Maß E=121.6 mm  [stored 0.39895 ft]; Maß F=132 mm  [stored 0.433071 ft]; Maß H=302 mm  [stored 0.990814 ft]; Maß K=134 mm; Maß M=158 mm; Maß Ø D=198 mm  [stored 0.649606 ft]; Maß Ø D1=196 mm  [stored 0.643045 ft]; Mindest-abstand (m)=11.0/>15.0/>15.0; Stutzen (Stk.)=1; Visible 1 Reihig=No; Visible 1 Stutzen=Yes; Visible 2 Reihig=No; Visible 2 Stutzen=No; Visible 3 Reihig=No; Visible 4 Reihig=Yes; x krit (m)=13.4/>15.0/>15.0; y (m)=2.9/3.8/4.9; Δp (Pa) 1=9/14/21; Δp (Pa) 2=13/20/29
- 1400_2-reihig mit Anschlusskasten: Gewicht (g/m)=5585; Index=1; Index L=10; Index Reihig=2; L=1400 mm; Maß B=120 mm  [stored 0.393701 ft]; Maß E=57.4 mm  [stored 0.18832 ft]; Maß F=67 mm; Maß H=242 mm  [stored 0.793963 ft]; Maß K=69 mm  [stored 0.226378 ft]; Maß M=92 mm  [stored 0.301837 ft]; Maß Ø D=138 mm  [stored 0.452756 ft]; Maß Ø D1=136 mm  [stored 0.446194 ft]; Mindest-abstand (m)=3.3/12.0/>15.0; Stutzen (Stk.)=1; Visible 1 Reihig=No; Visible 1 Stutzen=Yes; Visible 2 Reihig=Yes; Visible 2 Stutzen=No; Visible 3 Reihig=No; Visible 4 Reihig=No; x krit (m)=10.6/13.8/>15.0; y (m)=2.3/2.9/3.6; Δp (Pa) 1=12/18/27; Δp (Pa) 2=18/25/36
- 1400_3-reihig mit Anschlusskasten: Gewicht (g/m)=6979; Index=1; Index L=10; Index Reihig=3; L=1400 mm; Maß B=152 mm  [stored 0.498688 ft]; Maß E=89.5 mm  [stored 0.293635 ft]; Maß F=99 mm  [stored 0.324803 ft]; Maß H=262 mm  [stored 0.85958 ft]; Maß K=101 mm  [stored 0.331365 ft]; Maß M=126 mm  [stored 0.413386 ft]; Maß Ø D=158 mm; Maß Ø D1=156 mm; Mindest-abstand (m)=8.0/>15.0/>15.0; Stutzen (Stk.)=1; Visible 1 Reihig=No; Visible 1 Stutzen=Yes; Visible 2 Reihig=No; Visible 2 Stutzen=No; Visible 3 Reihig=Yes; Visible 4 Reihig=No; x krit (m)=12.3/15.0/>15.0; y (m)=2.7/3.4/4.5; Δp (Pa) 1=10/15/23; Δp (Pa) 2=15/22/33
- 1400_4-reihig mit Anschlusskasten: Gewicht (g/m)=8554; Index=1; Index L=10; Index Reihig=4; L=1400 mm; Maß B=184 mm  [stored 0.603675 ft]; Maß E=121.6 mm  [stored 0.39895 ft]; Maß F=132 mm  [stored 0.433071 ft]; Maß H=302 mm  [stored 0.990814 ft]; Maß K=134 mm; Maß M=158 mm; Maß Ø D=198 mm  [stored 0.649606 ft]; Maß Ø D1=196 mm  [stored 0.643045 ft]; Mindest-abstand (m)=11.0/>15.0/>15.0; Stutzen (Stk.)=1; Visible 1 Reihig=No; Visible 1 Stutzen=Yes; Visible 2 Reihig=No; Visible 2 Stutzen=No; Visible 3 Reihig=No; Visible 4 Reihig=Yes; x krit (m)=13.4/>15.0/>15.0; y (m)=2.9/3.8/4.9; Δp (Pa) 1=9/14/21; Δp (Pa) 2=13/20/29
- 1500_2-reihig mit Anschlusskasten: Gewicht (g/m)=5585; Index=1; Index L=11; Index Reihig=2; L=1500 mm; Maß B=120 mm  [stored 0.393701 ft]; Maß E=57.4 mm  [stored 0.18832 ft]; Maß F=67 mm; Maß H=242 mm  [stored 0.793963 ft]; Maß K=69 mm  [stored 0.226378 ft]; Maß M=92 mm  [stored 0.301837 ft]; Maß Ø D=138 mm  [stored 0.452756 ft]; Maß Ø D1=136 mm  [stored 0.446194 ft]; Mindest-abstand (m)=3.3/12.0/>15.0; Stutzen (Stk.)=1; Visible 1 Reihig=No; Visible 1 Stutzen=Yes; Visible 2 Reihig=Yes; Visible 2 Stutzen=No; Visible 3 Reihig=No; Visible 4 Reihig=No; x krit (m)=10.6/13.8/>15.0; y (m)=2.3/2.9/3.6; Δp (Pa) 1=12/18/27; Δp (Pa) 2=18/25/36
- 1500_3-reihig mit Anschlusskasten: Gewicht (g/m)=6979; Index=1; Index L=11; Index Reihig=3; L=1500 mm; Maß B=152 mm  [stored 0.498688 ft]; Maß E=89.5 mm  [stored 0.293635 ft]; Maß F=99 mm  [stored 0.324803 ft]; Maß H=262 mm  [stored 0.85958 ft]; Maß K=101 mm  [stored 0.331365 ft]; Maß M=126 mm  [stored 0.413386 ft]; Maß Ø D=158 mm; Maß Ø D1=156 mm; Mindest-abstand (m)=8.0/>15.0/>15.0; Stutzen (Stk.)=1; Visible 1 Reihig=No; Visible 1 Stutzen=Yes; Visible 2 Reihig=No; Visible 2 Stutzen=No; Visible 3 Reihig=Yes; Visible 4 Reihig=No; x krit (m)=12.3/15.0/>15.0; y (m)=2.7/3.4/4.5; Δp (Pa) 1=10/15/23; Δp (Pa) 2=15/22/33
- 1500_4-reihig mit Anschlusskasten: Gewicht (g/m)=8554; Index=1; Index L=11; Index Reihig=4; L=1500 mm; Maß B=184 mm  [stored 0.603675 ft]; Maß E=121.6 mm  [stored 0.39895 ft]; Maß F=132 mm  [stored 0.433071 ft]; Maß H=302 mm  [stored 0.990814 ft]; Maß K=134 mm; Maß M=158 mm; Maß Ø D=198 mm  [stored 0.649606 ft]; Maß Ø D1=196 mm  [stored 0.643045 ft]; Mindest-abstand (m)=11.0/>15.0/>15.0; Stutzen (Stk.)=1; Visible 1 Reihig=No; Visible 1 Stutzen=Yes; Visible 2 Reihig=No; Visible 2 Stutzen=No; Visible 3 Reihig=No; Visible 4 Reihig=Yes; x krit (m)=13.4/>15.0/>15.0; y (m)=2.9/3.8/4.9; Δp (Pa) 1=9/14/21; Δp (Pa) 2=13/20/29
- 1600_2-reihig mit Anschlusskasten: Gewicht (g/m)=5585; Index=2; Index L=12; Index Reihig=2; L=1600 mm; Maß B=120 mm  [stored 0.393701 ft]; Maß E=57.4 mm  [stored 0.18832 ft]; Maß F=67 mm; Maß H=242 mm  [stored 0.793963 ft]; Maß K=69 mm  [stored 0.226378 ft]; Maß M=92 mm  [stored 0.301837 ft]; Maß Ø D=138 mm  [stored 0.452756 ft]; Maß Ø D1=136 mm  [stored 0.446194 ft]; Mindest-abstand (m)=3.3/12.0/>15.0; Stutzen (Stk.)=2; Visible 1 Reihig=No; Visible 1 Stutzen=No; Visible 2 Reihig=Yes; Visible 2 Stutzen=Yes; Visible 3 Reihig=No; Visible 4 Reihig=No; x krit (m)=10.6/13.8/>15.0; y (m)=2.3/2.9/3.6; Δp (Pa) 1=12/18/27; Δp (Pa) 2=18/25/36
- 1600_3-reihig mit Anschlusskasten: Gewicht (g/m)=6979; Index=2; Index L=12; Index Reihig=3; L=1600 mm; Maß B=152 mm  [stored 0.498688 ft]; Maß E=89.5 mm  [stored 0.293635 ft]; Maß F=99 mm  [stored 0.324803 ft]; Maß H=262 mm  [stored 0.85958 ft]; Maß K=101 mm  [stored 0.331365 ft]; Maß M=126 mm  [stored 0.413386 ft]; Maß Ø D=158 mm; Maß Ø D1=156 mm; Mindest-abstand (m)=8.0/>15.0/>15.0; Stutzen (Stk.)=2; Visible 1 Reihig=No; Visible 1 Stutzen=No; Visible 2 Reihig=No; Visible 2 Stutzen=Yes; Visible 3 Reihig=Yes; Visible 4 Reihig=No; x krit (m)=12.3/15.0/>15.0; y (m)=2.7/3.4/4.5; Δp (Pa) 1=10/15/23; Δp (Pa) 2=15/22/33
- 1600_4-reihig mit Anschlusskasten: Gewicht (g/m)=8554; Index=2; Index L=12; Index Reihig=4; L=1600 mm; Maß B=184 mm  [stored 0.603675 ft]; Maß E=121.6 mm  [stored 0.39895 ft]; Maß F=132 mm  [stored 0.433071 ft]; Maß H=302 mm  [stored 0.990814 ft]; Maß K=134 mm; Maß M=158 mm; Maß Ø D=198 mm  [stored 0.649606 ft]; Maß Ø D1=196 mm  [stored 0.643045 ft]; Mindest-abstand (m)=11.0/>15.0/>15.0; Stutzen (Stk.)=2; Visible 1 Reihig=No; Visible 1 Stutzen=No; Visible 2 Reihig=No; Visible 2 Stutzen=Yes; Visible 3 Reihig=No; Visible 4 Reihig=Yes; x krit (m)=13.4/>15.0/>15.0; y (m)=2.9/3.8/4.9; Δp (Pa) 1=9/14/21; Δp (Pa) 2=13/20/29
- 1700_2-reihig mit Anschlusskasten: Gewicht (g/m)=5585; Index=2; Index L=13; Index Reihig=2; L=1700 mm; Maß B=120 mm  [stored 0.393701 ft]; Maß E=57.4 mm  [stored 0.18832 ft]; Maß F=67 mm; Maß H=242 mm  [stored 0.793963 ft]; Maß K=69 mm  [stored 0.226378 ft]; Maß M=92 mm  [stored 0.301837 ft]; Maß Ø D=138 mm  [stored 0.452756 ft]; Maß Ø D1=136 mm  [stored 0.446194 ft]; Mindest-abstand (m)=3.3/12.0/>15.0; Stutzen (Stk.)=2; Visible 1 Reihig=No; Visible 1 Stutzen=No; Visible 2 Reihig=Yes; Visible 2 Stutzen=Yes; Visible 3 Reihig=No; Visible 4 Reihig=No; x krit (m)=10.6/13.8/>15.0; y (m)=2.3/2.9/3.6; Δp (Pa) 1=12/18/27; Δp (Pa) 2=18/25/36
- 1700_3-reihig mit Anschlusskasten: Gewicht (g/m)=6979; Index=2; Index L=13; Index Reihig=3; L=1700 mm; Maß B=152 mm  [stored 0.498688 ft]; Maß E=89.5 mm  [stored 0.293635 ft]; Maß F=99 mm  [stored 0.324803 ft]; Maß H=262 mm  [stored 0.85958 ft]; Maß K=101 mm  [stored 0.331365 ft]; Maß M=126 mm  [stored 0.413386 ft]; Maß Ø D=158 mm; Maß Ø D1=156 mm; Mindest-abstand (m)=8.0/>15.0/>15.0; Stutzen (Stk.)=2; Visible 1 Reihig=No; Visible 1 Stutzen=No; Visible 2 Reihig=No; Visible 2 Stutzen=Yes; Visible 3 Reihig=Yes; Visible 4 Reihig=No; x krit (m)=12.3/15.0/>15.0; y (m)=2.7/3.4/4.5; Δp (Pa) 1=10/15/23; Δp (Pa) 2=15/22/33
- 1700_4-reihig mit Anschlusskasten: Gewicht (g/m)=8554; Index=2; Index L=13; Index Reihig=4; L=1700 mm; Maß B=184 mm  [stored 0.603675 ft]; Maß E=121.6 mm  [stored 0.39895 ft]; Maß F=132 mm  [stored 0.433071 ft]; Maß H=302 mm  [stored 0.990814 ft]; Maß K=134 mm; Maß M=158 mm; Maß Ø D=198 mm  [stored 0.649606 ft]; Maß Ø D1=196 mm  [stored 0.643045 ft]; Mindest-abstand (m)=11.0/>15.0/>15.0; Stutzen (Stk.)=2; Visible 1 Reihig=No; Visible 1 Stutzen=No; Visible 2 Reihig=No; Visible 2 Stutzen=Yes; Visible 3 Reihig=No; Visible 4 Reihig=Yes; x krit (m)=13.4/>15.0/>15.0; y (m)=2.9/3.8/4.9; Δp (Pa) 1=9/14/21; Δp (Pa) 2=13/20/29
- 1800_2-reihig mit Anschlusskasten: Gewicht (g/m)=5585; Index=2; Index L=14; Index Reihig=2; L=1800 mm; Maß B=120 mm  [stored 0.393701 ft]; Maß E=57.4 mm  [stored 0.18832 ft]; Maß F=67 mm; Maß H=242 mm  [stored 0.793963 ft]; Maß K=69 mm  [stored 0.226378 ft]; Maß M=92 mm  [stored 0.301837 ft]; Maß Ø D=138 mm  [stored 0.452756 ft]; Maß Ø D1=136 mm  [stored 0.446194 ft]; Mindest-abstand (m)=3.3/12.0/>15.0; Stutzen (Stk.)=2; Visible 1 Reihig=No; Visible 1 Stutzen=No; Visible 2 Reihig=Yes; Visible 2 Stutzen=Yes; Visible 3 Reihig=No; Visible 4 Reihig=No; x krit (m)=10.6/13.8/>15.0; y (m)=2.3/2.9/3.6; Δp (Pa) 1=12/18/27; Δp (Pa) 2=18/25/36
- 1800_3-reihig mit Anschlusskasten: Gewicht (g/m)=6979; Index=2; Index L=14; Index Reihig=3; L=1800 mm; Maß B=152 mm  [stored 0.498688 ft]; Maß E=89.5 mm  [stored 0.293635 ft]; Maß F=99 mm  [stored 0.324803 ft]; Maß H=262 mm  [stored 0.85958 ft]; Maß K=101 mm  [stored 0.331365 ft]; Maß M=126 mm  [stored 0.413386 ft]; Maß Ø D=158 mm; Maß Ø D1=156 mm; Mindest-abstand (m)=8.0/>15.0/>15.0; Stutzen (Stk.)=2; Visible 1 Reihig=No; Visible 1 Stutzen=No; Visible 2 Reihig=No; Visible 2 Stutzen=Yes; Visible 3 Reihig=Yes; Visible 4 Reihig=No; x krit (m)=12.3/15.0/>15.0; y (m)=2.7/3.4/4.5; Δp (Pa) 1=10/15/23; Δp (Pa) 2=15/22/33
- 1800_4-reihig mit Anschlusskasten: Gewicht (g/m)=8554; Index=2; Index L=14; Index Reihig=4; L=1800 mm; Maß B=184 mm  [stored 0.603675 ft]; Maß E=121.6 mm  [stored 0.39895 ft]; Maß F=132 mm  [stored 0.433071 ft]; Maß H=302 mm  [stored 0.990814 ft]; Maß K=134 mm; Maß M=158 mm; Maß Ø D=198 mm  [stored 0.649606 ft]; Maß Ø D1=196 mm  [stored 0.643045 ft]; Mindest-abstand (m)=11.0/>15.0/>15.0; Stutzen (Stk.)=2; Visible 1 Reihig=No; Visible 1 Stutzen=No; Visible 2 Reihig=No; Visible 2 Stutzen=Yes; Visible 3 Reihig=No; Visible 4 Reihig=Yes; x krit (m)=13.4/>15.0/>15.0; y (m)=2.9/3.8/4.9; Δp (Pa) 1=9/14/21; Δp (Pa) 2=13/20/29
- 1900_2-reihig mit Anschlusskasten: Gewicht (g/m)=5585; Index=2; Index L=15; Index Reihig=2; L=1900 mm; Maß B=120 mm  [stored 0.393701 ft]; Maß E=57.4 mm  [stored 0.18832 ft]; Maß F=67 mm; Maß H=242 mm  [stored 0.793963 ft]; Maß K=69 mm  [stored 0.226378 ft]; Maß M=92 mm  [stored 0.301837 ft]; Maß Ø D=138 mm  [stored 0.452756 ft]; Maß Ø D1=136 mm  [stored 0.446194 ft]; Mindest-abstand (m)=3.3/12.0/>15.0; Stutzen (Stk.)=2; Visible 1 Reihig=Yes; Visible 1 Stutzen=No; Visible 2 Reihig=No; Visible 2 Stutzen=Yes; Visible 3 Reihig=No; Visible 4 Reihig=No; x krit (m)=10.6/13.8/>15.0; y (m)=2.3/2.9/3.6; Δp (Pa) 1=12/18/27; Δp (Pa) 2=18/25/36
- 1900_3-reihig mit Anschlusskasten: Gewicht (g/m)=6979; Index=2; Index L=15; Index Reihig=3; L=1900 mm; Maß B=152 mm  [stored 0.498688 ft]; Maß E=89.5 mm  [stored 0.293635 ft]; Maß F=99 mm  [stored 0.324803 ft]; Maß H=262 mm  [stored 0.85958 ft]; Maß K=101 mm  [stored 0.331365 ft]; Maß M=126 mm  [stored 0.413386 ft]; Maß Ø D=158 mm; Maß Ø D1=156 mm; Mindest-abstand (m)=8.0/>15.0/>15.0; Stutzen (Stk.)=2; Visible 1 Reihig=No; Visible 1 Stutzen=No; Visible 2 Reihig=No; Visible 2 Stutzen=Yes; Visible 3 Reihig=Yes; Visible 4 Reihig=No; x krit (m)=12.3/15.0/>15.0; y (m)=2.7/3.4/4.5; Δp (Pa) 1=10/15/23; Δp (Pa) 2=15/22/33
- 1900_4-reihig mit Anschlusskasten: Gewicht (g/m)=8554; Index=2; Index L=15; Index Reihig=4; L=1900 mm; Maß B=184 mm  [stored 0.603675 ft]; Maß E=121.6 mm  [stored 0.39895 ft]; Maß F=132 mm  [stored 0.433071 ft]; Maß H=302 mm  [stored 0.990814 ft]; Maß K=134 mm; Maß M=158 mm; Maß Ø D=198 mm  [stored 0.649606 ft]; Maß Ø D1=196 mm  [stored 0.643045 ft]; Mindest-abstand (m)=11.0/>15.0/>15.0; Stutzen (Stk.)=2; Visible 1 Reihig=No; Visible 1 Stutzen=No; Visible 2 Reihig=No; Visible 2 Stutzen=Yes; Visible 3 Reihig=No; Visible 4 Reihig=Yes; x krit (m)=13.4/>15.0/>15.0; y (m)=2.9/3.8/4.9; Δp (Pa) 1=9/14/21; Δp (Pa) 2=13/20/29
- 2000_2-reihig mit Anschlusskasten: Gewicht (g/m)=5585; Index=2; Index L=16; Index Reihig=2; L=2000 mm; Maß B=120 mm  [stored 0.393701 ft]; Maß E=57.4 mm  [stored 0.18832 ft]; Maß F=67 mm; Maß H=242 mm  [stored 0.793963 ft]; Maß K=69 mm  [stored 0.226378 ft]; Maß M=92 mm  [stored 0.301837 ft]; Maß Ø D=138 mm  [stored 0.452756 ft]; Maß Ø D1=136 mm  [stored 0.446194 ft]; Mindest-abstand (m)=3.3/12.0/>15.0; Stutzen (Stk.)=2; Visible 1 Reihig=No; Visible 1 Stutzen=No; Visible 2 Reihig=Yes; Visible 2 Stutzen=Yes; Visible 3 Reihig=No; Visible 4 Reihig=No; x krit (m)=10.6/13.8/>15.0; y (m)=2.3/2.9/3.6; Δp (Pa) 1=12/18/27; Δp (Pa) 2=18/25/36
- 2000_3-reihig mit Anschlusskasten: Gewicht (g/m)=6979; Index=2; Index L=16; Index Reihig=3; L=2000 mm; Maß B=152 mm  [stored 0.498688 ft]; Maß E=89.5 mm  [stored 0.293635 ft]; Maß F=99 mm  [stored 0.324803 ft]; Maß H=262 mm  [stored 0.85958 ft]; Maß K=101 mm  [stored 0.331365 ft]; Maß M=126 mm  [stored 0.413386 ft]; Maß Ø D=158 mm; Maß Ø D1=156 mm; Mindest-abstand (m)=8.0/>15.0/>15.0; Stutzen (Stk.)=2; Visible 1 Reihig=No; Visible 1 Stutzen=No; Visible 2 Reihig=No; Visible 2 Stutzen=Yes; Visible 3 Reihig=Yes; Visible 4 Reihig=No; x krit (m)=12.3/15.0/>15.0; y (m)=2.7/3.4/4.5; Δp (Pa) 1=10/15/23; Δp (Pa) 2=15/22/33
- 2000_4-reihig mit Anschlusskasten: Gewicht (g/m)=8554; Index=2; Index L=16; Index Reihig=4; L=2000 mm; Maß B=184 mm  [stored 0.603675 ft]; Maß E=121.6 mm  [stored 0.39895 ft]; Maß F=132 mm  [stored 0.433071 ft]; Maß H=302 mm  [stored 0.990814 ft]; Maß K=134 mm; Maß M=158 mm; Maß Ø D=198 mm  [stored 0.649606 ft]; Maß Ø D1=196 mm  [stored 0.643045 ft]; Mindest-abstand (m)=11.0/>15.0/>15.0; Stutzen (Stk.)=2; Visible 1 Reihig=No; Visible 1 Stutzen=No; Visible 2 Reihig=No; Visible 2 Stutzen=Yes; Visible 3 Reihig=No; Visible 4 Reihig=Yes; x krit (m)=13.4/>15.0/>15.0; y (m)=2.9/3.8/4.9; Δp (Pa) 1=9/14/21; Δp (Pa) 2=13/20/29

note: [stored X ft] marks values corroborated as IEEE doubles in the binary element streams (Revit-internal decimal feet)

## geometry (parser evidence)
native form markers: Sweep x13
no freeform markers — native parametric forms only
